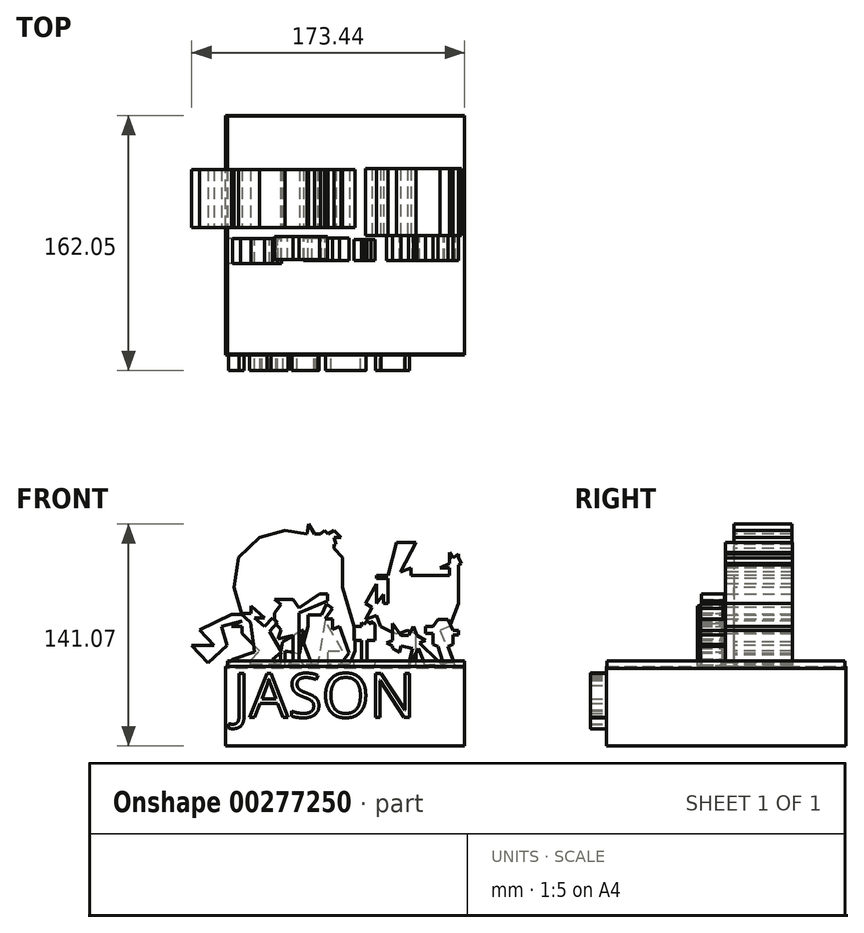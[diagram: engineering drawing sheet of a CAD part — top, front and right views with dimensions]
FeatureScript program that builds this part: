
annotation { "Feature Type Name" : "Feature", "Feature Type Description" : "" }
export const myFeature = defineFeature(function(context is Context, id is Id, definition is map)
    precondition{}
    {
        {
            var Q0;
            Q0=qCreatedBy(makeId("Front.planeOp"),FACE);
            var sketch = newSketch(context, id + "F0", { "sketchPlane" : qUnion([Q0])});
            skLineSegment(sketch, "E0.bottom", {"start": v(-75.76, -25.37) * mm, "end": v(76, -25.37) * mm});
            skLineSegment(sketch, "E0.top", {"start": v(-75.76, -75.88) * mm, "end": v(76, -75.88) * mm});
            skLineSegment(sketch, "E0.left", {"start": v(-75.76, -25.37) * mm, "end": v(-75.76, -75.88) * mm});
            skLineSegment(sketch, "E0.right", {"start": v(76, -25.37) * mm, "end": v(76, -75.88) * mm});
            skSolve(sketch);
        }
        {
            var Q0;
            Q0 = qSketchRegion(id + "F0", true);
            extrude(context, id + "F1", {"entities" : qUnion([Q0]), "depth" : 75.7 * mm, "hasSecondDirection" : true, "secondDirectionOppositeDirection" : true, "secondDirectionDepth" : 76.45 * mm});
        }
        {
            var Q0;
            Q0=qCreatedBy(makeId("Front.planeOp"),FACE);
            var sketch = newSketch(context, id + "F2", { "sketchPlane" : qUnion([Q0])});
            skLineSegment(sketch, "E1", {"start": v(-59.85, -23.92) * mm, "end": v(-59.85, -21.49) * mm});
            skLineSegment(sketch, "E2", {"start": v(-59.85, -21.49) * mm, "end": v(-54.02, -15.42) * mm});
            skLineSegment(sketch, "E3", {"start": v(-54.02, -15.42) * mm, "end": v(-65.45, -4.45) * mm});
            skLineSegment(sketch, "E4", {"start": v(-65.45, -4.45) * mm, "end": v(-65.45, 0) * mm});
            skLineSegment(sketch, "E5", {"start": v(-65.45, 0) * mm, "end": v(-71.9, 0) * mm});
            skLineSegment(sketch, "E6", {"start": v(-71.9, 0) * mm, "end": v(-65.45, 3.76) * mm});
            skLineSegment(sketch, "E7", {"start": v(-65.45, 3.76) * mm, "end": v(-78.3, 0) * mm});
            skLineSegment(sketch, "E8", {"start": v(-78.3, 0) * mm, "end": v(-74.8, -11.96) * mm});
            skLineSegment(sketch, "E9", {"start": v(-74.8, -11.96) * mm, "end": v(-86.8, -23.19) * mm});
            skLineSegment(sketch, "E10", {"start": v(-86.8, -23.19) * mm, "end": v(-97.31, -11.96) * mm});
            skLineSegment(sketch, "E11", {"start": v(-97.31, -11.96) * mm, "end": v(-82.92, -11.96) * mm});
            skLineSegment(sketch, "E12", {"start": v(-82.92, -11.96) * mm, "end": v(-92.3, -1.93) * mm});
            skLineSegment(sketch, "E13", {"start": v(-92.3, -1.93) * mm, "end": v(-71.9, 7.9) * mm});
            skLineSegment(sketch, "E14", {"start": v(-71.9, 7.9) * mm, "end": v(-65.45, 7.9) * mm});
            skLineSegment(sketch, "E15", {"start": v(-65.45, 7.9) * mm, "end": v(-70.43, 24.9) * mm});
            skLineSegment(sketch, "E16", {"start": v(-70.43, 24.9) * mm, "end": v(-67.62, 43.83) * mm});
            skLineSegment(sketch, "E17", {"start": v(-67.62, 43.83) * mm, "end": v(-54.02, 56.55) * mm});
            skLineSegment(sketch, "E18", {"start": v(-54.02, 56.55) * mm, "end": v(-38.04, 61.23) * mm});
            skLineSegment(sketch, "E19", {"start": v(-38.04, 61.23) * mm, "end": v(-24.16, 58.88) * mm});
            skLineSegment(sketch, "E20", {"start": v(-24.16, 58.88) * mm, "end": v(-23.1, 65.19) * mm});
            skLineSegment(sketch, "E21", {"start": v(-23.1, 65.19) * mm, "end": v(-19.41, 58.88) * mm});
            skLineSegment(sketch, "E22", {"start": v(-19.41, 58.88) * mm, "end": v(-15.5, 58.88) * mm});
            skLineSegment(sketch, "E23", {"start": v(-15.5, 58.88) * mm, "end": v(-13, 61.23) * mm});
            skLineSegment(sketch, "E24", {"start": v(-13, 61.23) * mm, "end": v(-10.8, 58.88) * mm});
            skLineSegment(sketch, "E25", {"start": v(-10.8, 58.88) * mm, "end": v(-6.78, 61.23) * mm});
            skLineSegment(sketch, "E26", {"start": v(-6.78, 61.23) * mm, "end": v(-2.4, 56.55) * mm});
            skLineSegment(sketch, "E27", {"start": v(-2.4, 56.55) * mm, "end": v(-6.78, 56.55) * mm});
            skLineSegment(sketch, "E28", {"start": v(-6.78, 56.55) * mm, "end": v(-5.55, 52.34) * mm});
            skLineSegment(sketch, "E29", {"start": v(-5.55, 52.34) * mm, "end": v(-6.78, 52.34) * mm});
            skLineSegment(sketch, "E30", {"start": v(-6.78, 52.34) * mm, "end": v(-6.78, 49.66) * mm});
            skLineSegment(sketch, "E31", {"start": v(-6.78, 49.66) * mm, "end": v(-1.33, 43.83) * mm});
            skLineSegment(sketch, "E32", {"start": v(-1.33, 43.83) * mm, "end": v(-1.33, 24.9) * mm});
            skLineSegment(sketch, "E33", {"start": v(-1.33, 24.9) * mm, "end": v(6.53, -1.93) * mm});
            skLineSegment(sketch, "E34", {"start": v(6.53, -1.93) * mm, "end": v(6.53, -15.42) * mm});
            skLineSegment(sketch, "E35", {"start": v(6.53, -15.42) * mm, "end": v(3.02, -23.92) * mm});
            skLineSegment(sketch, "E36", {"start": v(3.02, -23.92) * mm, "end": v(-10.8, -23.92) * mm});
            skLineSegment(sketch, "E37", {"start": v(-10.8, -23.92) * mm, "end": v(-10.8, -15.42) * mm});
            skLineSegment(sketch, "E38", {"start": v(-10.8, -15.42) * mm, "end": v(-1.33, -15.42) * mm});
            skLineSegment(sketch, "E39", {"start": v(-1.33, -15.42) * mm, "end": v(-12.52, 3.76) * mm});
            skLineSegment(sketch, "E40", {"start": v(-12.52, 3.76) * mm, "end": v(-17.2, -23.92) * mm});
            skLineSegment(sketch, "E41", {"start": v(-17.2, -23.92) * mm, "end": v(-38.04, -23.92) * mm});
            skLineSegment(sketch, "E42", {"start": v(-38.04, -23.92) * mm, "end": v(-38.04, -15.42) * mm});
            skLineSegment(sketch, "E43", {"start": v(-38.04, -15.42) * mm, "end": v(-28.87, -16.97) * mm});
            skLineSegment(sketch, "E44", {"start": v(-28.87, -16.97) * mm, "end": v(-26.32, -1.93) * mm});
            skLineSegment(sketch, "E45", {"start": v(-26.32, -1.93) * mm, "end": v(-39.52, -9.63) * mm});
            skLineSegment(sketch, "E46", {"start": v(-39.52, -9.63) * mm, "end": v(-40.93, -17.97) * mm});
            skLineSegment(sketch, "E47", {"start": v(-40.93, -17.97) * mm, "end": v(-40.93, -23.92) * mm});
            skLineSegment(sketch, "E48", {"start": v(-40.93, -23.92) * mm, "end": v(-59.85, -23.92) * mm});
            skSolve(sketch);
        }
        {
            var Q0;
            Q0 = qSketchRegion(id + "F2", true);
            extrude(context, id + "F3", {"entities" : qUnion([Q0]), "oppositeDirection" : true, "depth" : 42.16 * mm, "hasSecondDirection" : true, "secondDirectionOppositeDirection" : true, "secondDirectionDepth" : 5.33 * mm});
        }
        {
            var Q0;
            Q0=qCreatedBy(makeId("Front.planeOp"),FACE);
            var sketch = newSketch(context, id + "F4", { "sketchPlane" : qUnion([Q0])});
            skLineSegment(sketch, "E49", {"start": v(45.05, -25.13) * mm, "end": v(45.05, -4.74) * mm});
            skLineSegment(sketch, "E50", {"start": v(45.05, -4.74) * mm, "end": v(39.7, -2.3) * mm});
            skLineSegment(sketch, "E51", {"start": v(39.7, -2.3) * mm, "end": v(32.9, -4.74) * mm});
            skLineSegment(sketch, "E52", {"start": v(32.9, -4.74) * mm, "end": v(22.7, 0) * mm});
            skLineSegment(sketch, "E53", {"start": v(22.7, 0) * mm, "end": v(20.04, 7.16) * mm});
            skLineSegment(sketch, "E54", {"start": v(20.04, 7.16) * mm, "end": v(13.01, 4.54) * mm});
            skLineSegment(sketch, "E55", {"start": v(13.01, 4.54) * mm, "end": v(17.37, 12.26) * mm});
            skLineSegment(sketch, "E56", {"start": v(17.37, 12.26) * mm, "end": v(13.01, 14.72) * mm});
            skLineSegment(sketch, "E57", {"start": v(13.01, 14.72) * mm, "end": v(20.04, 27.17) * mm});
            skLineSegment(sketch, "E58", {"start": v(20.04, 27.17) * mm, "end": v(20.04, 14.72) * mm});
            skLineSegment(sketch, "E59", {"start": v(20.04, 14.72) * mm, "end": v(24.4, 20.52) * mm});
            skLineSegment(sketch, "E60", {"start": v(24.4, 20.52) * mm, "end": v(24.4, 14.72) * mm});
            skLineSegment(sketch, "E61", {"start": v(24.4, 14.72) * mm, "end": v(27.57, 14.72) * mm});
            skLineSegment(sketch, "E62", {"start": v(27.57, 14.72) * mm, "end": v(27.57, 30.47) * mm});
            skLineSegment(sketch, "E63", {"start": v(27.57, 30.47) * mm, "end": v(20.04, 30.47) * mm});
            skLineSegment(sketch, "E64", {"start": v(20.04, 30.47) * mm, "end": v(20.04, 32.66) * mm});
            skLineSegment(sketch, "E65", {"start": v(20.04, 32.66) * mm, "end": v(27.57, 32.66) * mm});
            skLineSegment(sketch, "E66", {"start": v(27.57, 32.66) * mm, "end": v(32.9, 53.54) * mm});
            skLineSegment(sketch, "E67", {"start": v(32.9, 53.54) * mm, "end": v(45.05, 53.54) * mm});
            skLineSegment(sketch, "E68", {"start": v(45.05, 53.54) * mm, "end": v(35.34, 34.6) * mm});
            skLineSegment(sketch, "E69", {"start": v(35.34, 34.6) * mm, "end": v(42.14, 37.27) * mm});
            skLineSegment(sketch, "E70", {"start": v(42.14, 37.27) * mm, "end": v(42.14, 32.66) * mm});
            skLineSegment(sketch, "E71", {"start": v(42.14, 32.66) * mm, "end": v(66.42, 32.66) * mm});
            skLineSegment(sketch, "E72", {"start": v(66.42, 32.66) * mm, "end": v(66.42, 37.27) * mm});
            skLineSegment(sketch, "E73", {"start": v(66.42, 37.27) * mm, "end": v(60.59, 37.27) * mm});
            skLineSegment(sketch, "E74", {"start": v(60.59, 37.27) * mm, "end": v(66.42, 40.19) * mm});
            skLineSegment(sketch, "E75", {"start": v(66.42, 40.19) * mm, "end": v(66.42, 46.99) * mm});
            skLineSegment(sketch, "E76", {"start": v(66.42, 46.99) * mm, "end": v(68.85, 43.59) * mm});
            skPoint(sketch, "E76.endSnap0", {"position": v(66.42, 43.59) * mm});
            skLineSegment(sketch, "E77", {"start": v(68.85, 43.59) * mm, "end": v(72.31, 46.06) * mm});
            skLineSegment(sketch, "E78", {"start": v(72.31, 46.06) * mm, "end": v(72.31, 43.59) * mm});
            skLineSegment(sketch, "E79", {"start": v(72.31, 43.59) * mm, "end": v(74.19, 40.19) * mm});
            skLineSegment(sketch, "E80", {"start": v(74.19, 40.19) * mm, "end": v(72.31, 39.15) * mm});
            skLineSegment(sketch, "E81", {"start": v(72.31, 39.15) * mm, "end": v(72.31, 32.66) * mm});
            skLineSegment(sketch, "E82", {"start": v(72.31, 32.66) * mm, "end": v(72.31, 14.72) * mm});
            skLineSegment(sketch, "E83", {"start": v(72.31, 14.72) * mm, "end": v(66.42, 0) * mm});
            skLineSegment(sketch, "E84", {"start": v(66.42, 0) * mm, "end": v(60.59, -2.3) * mm});
            skLineSegment(sketch, "E85", {"start": v(60.59, -2.3) * mm, "end": v(68.85, -23.16) * mm});
            skLineSegment(sketch, "E86", {"start": v(68.85, -23.16) * mm, "end": v(45.05, -25.13) * mm});
            skSolve(sketch);
        }
        {
            var Q0;
            Q0 = qSketchRegion(id + "F4", true);
            extrude(context, id + "F5", {"entities" : qUnion([Q0]), "oppositeDirection" : true, "depth" : 42.67 * mm});
        }
        {
            var Q0;
            Q0=qCreatedBy(makeId("Front.planeOp"),FACE);
            var sketch = newSketch(context, id + "F6", { "sketchPlane" : qUnion([Q0])});
            skLineSegment(sketch, "E87", {"start": v(70.3, -25.62) * mm, "end": v(65.45, -12.5) * mm});
            skLineSegment(sketch, "E88", {"start": v(65.45, -12.5) * mm, "end": v(68.74, -11.28) * mm});
            skLineSegment(sketch, "E89", {"start": v(68.74, -11.28) * mm, "end": v(68.74, -5.22) * mm});
            skLineSegment(sketch, "E90", {"start": v(68.74, -5.22) * mm, "end": v(72.25, -5.22) * mm});
            skLineSegment(sketch, "E91", {"start": v(72.25, -5.22) * mm, "end": v(72.25, -2.3) * mm});
            skLineSegment(sketch, "E92", {"start": v(72.25, -2.3) * mm, "end": v(68.74, -2.3) * mm});
            skLineSegment(sketch, "E93", {"start": v(68.74, -2.3) * mm, "end": v(65.45, 4.74) * mm});
            skLineSegment(sketch, "E94", {"start": v(65.45, 4.74) * mm, "end": v(59.13, 4.74) * mm});
            skLineSegment(sketch, "E95", {"start": v(59.13, 4.74) * mm, "end": v(55.98, 0) * mm});
            skLineSegment(sketch, "E96", {"start": v(55.98, 0) * mm, "end": v(51.12, 0) * mm});
            skLineSegment(sketch, "E97", {"start": v(51.12, 0) * mm, "end": v(51.12, -4.25) * mm});
            skLineSegment(sketch, "E98", {"start": v(51.12, -4.25) * mm, "end": v(55.98, -4.25) * mm});
            skLineSegment(sketch, "E99", {"start": v(55.98, -4.25) * mm, "end": v(55.98, -11.28) * mm});
            skLineSegment(sketch, "E100", {"start": v(55.98, -11.28) * mm, "end": v(59.13, -12.5) * mm});
            skLineSegment(sketch, "E101", {"start": v(59.13, -12.5) * mm, "end": v(63.26, -25.37) * mm});
            skLineSegment(sketch, "E102", {"start": v(63.26, -25.37) * mm, "end": v(70.3, -25.62) * mm});
            skSolve(sketch);
        }
        {
            var Q0;
            Q0 = qSketchRegion(id + "F6", true);
            extrude(context, id + "F7", {"entities" : qUnion([Q0]), "depth" : 15.75 * mm});
        }
        {
            var Q0;
            Q0=qCreatedBy(makeId("Front.planeOp"),FACE);
            var sketch = newSketch(context, id + "F8", { "sketchPlane" : qUnion([Q0])});
            skLineSegment(sketch, "E103", {"start": v(51.6, -26.1) * mm, "end": v(46.75, -13.96) * mm});
            skLineSegment(sketch, "E104", {"start": v(46.75, -13.96) * mm, "end": v(40.44, -25.13) * mm});
            skLineSegment(sketch, "E105", {"start": v(40.44, -25.13) * mm, "end": v(42.86, -13.96) * mm});
            skLineSegment(sketch, "E106", {"start": v(42.86, -13.96) * mm, "end": v(35.59, -12.38) * mm});
            skLineSegment(sketch, "E107", {"start": v(35.59, -12.38) * mm, "end": v(34.7, -16.46) * mm});
            skLineSegment(sketch, "E108", {"start": v(34.7, -16.46) * mm, "end": v(30.27, -13.96) * mm});
            skLineSegment(sketch, "E109", {"start": v(30.27, -13.96) * mm, "end": v(30.27, -12.38) * mm});
            skLineSegment(sketch, "E110", {"start": v(30.27, -12.38) * mm, "end": v(26.5, -10.25) * mm});
            skLineSegment(sketch, "E111", {"start": v(26.5, -10.25) * mm, "end": v(30.27, -8.74) * mm});
            skLineSegment(sketch, "E112", {"start": v(30.27, -8.74) * mm, "end": v(30.27, 2.06) * mm});
            skLineSegment(sketch, "E113", {"start": v(30.27, 2.06) * mm, "end": v(35.59, -5.7) * mm});
            skLineSegment(sketch, "E114", {"start": v(35.59, -5.7) * mm, "end": v(40.44, -5.7) * mm});
            skLineSegment(sketch, "E115", {"start": v(40.44, -5.7) * mm, "end": v(43.66, 0) * mm});
            skLineSegment(sketch, "E116", {"start": v(43.66, 0) * mm, "end": v(45.94, -5.7) * mm});
            skLineSegment(sketch, "E117", {"start": v(45.94, -5.7) * mm, "end": v(51.3, -8.74) * mm});
            skLineSegment(sketch, "E118", {"start": v(51.3, -8.74) * mm, "end": v(47.53, -10.25) * mm});
            skLineSegment(sketch, "E119", {"start": v(47.53, -10.25) * mm, "end": v(62.53, -25.13) * mm});
            skLineSegment(sketch, "E120", {"start": v(62.53, -25.13) * mm, "end": v(51.6, -26.1) * mm});
            skSolve(sketch);
        }
        {
            var Q0;
            Q0 = qSketchRegion(id + "F8", true);
            extrude(context, id + "F9", {"entities" : qUnion([Q0]), "depth" : 15.75 * mm});
        }
        {
            var Q0;
            Q0=qCreatedBy(makeId("Front.planeOp"),FACE);
            var sketch = newSketch(context, id + "F10", { "sketchPlane" : qUnion([Q0])});
            skLineSegment(sketch, "E121", {"start": v(5.71, -25.37) * mm, "end": v(5.71, -21.98) * mm});
            skLineSegment(sketch, "E122", {"start": v(5.71, -21.98) * mm, "end": v(10.57, -21.98) * mm});
            skLineSegment(sketch, "E123", {"start": v(10.57, -21.98) * mm, "end": v(10.57, -8.86) * mm});
            skLineSegment(sketch, "E124", {"start": v(10.57, -8.86) * mm, "end": v(5.71, -8.86) * mm});
            skLineSegment(sketch, "E125", {"start": v(5.71, -8.86) * mm, "end": v(5.71, 0) * mm});
            skLineSegment(sketch, "E126", {"start": v(5.71, 0) * mm, "end": v(10.57, 0) * mm});
            skLineSegment(sketch, "E127", {"start": v(10.57, 0) * mm, "end": v(10.57, 2.8) * mm});
            skLineSegment(sketch, "E128", {"start": v(10.57, 2.8) * mm, "end": v(13.73, 0) * mm});
            skLineSegment(sketch, "E129", {"start": v(13.73, 0) * mm, "end": v(12.15, 1.4) * mm});
            skLineSegment(sketch, "E130", {"start": v(12.15, 1.4) * mm, "end": v(14.1, 3.61) * mm});
            skLineSegment(sketch, "E131", {"start": v(14.1, 3.61) * mm, "end": v(16.61, 1.4) * mm});
            skLineSegment(sketch, "E132", {"start": v(16.61, 1.4) * mm, "end": v(16.61, 3.61) * mm});
            skLineSegment(sketch, "E133", {"start": v(16.61, 3.61) * mm, "end": v(19.12, 1.4) * mm});
            skLineSegment(sketch, "E134", {"start": v(19.12, 1.4) * mm, "end": v(19.12, -8.86) * mm});
            skLineSegment(sketch, "E135", {"start": v(19.12, -8.86) * mm, "end": v(14.1, -8.86) * mm});
            skLineSegment(sketch, "E136", {"start": v(14.1, -8.86) * mm, "end": v(14.1, -21.98) * mm});
            skLineSegment(sketch, "E137", {"start": v(14.1, -21.98) * mm, "end": v(19.12, -21.98) * mm});
            skLineSegment(sketch, "E138", {"start": v(19.12, -21.98) * mm, "end": v(18.82, -24.65) * mm});
            skLineSegment(sketch, "E139", {"start": v(18.82, -24.65) * mm, "end": v(5.71, -25.37) * mm});
            skSolve(sketch);
        }
        {
            var Q0;
            Q0 = qSketchRegion(id + "F10", true);
            extrude(context, id + "F11", {"entities" : qUnion([Q0]), "operationType" : NewBodyOperationType.ADD, "depth" : 15.75 * mm, "hasSecondDirection" : true, "secondDirectionOppositeDirection" : false, "secondDirectionDepth" : 2.54 * mm});
        }
        {
            var Q0;
            Q0=qCreatedBy(makeId("Front.planeOp"),FACE);
            var sketch = newSketch(context, id + "F12", { "sketchPlane" : qUnion([Q0])});
            skLineSegment(sketch, "E140", {"start": v(-3.52, -24.89) * mm, "end": v(2.8, -16.63) * mm});
            skLineSegment(sketch, "E141", {"start": v(2.8, -16.63) * mm, "end": v(-3.27, 0) * mm});
            skLineSegment(sketch, "E142", {"start": v(-3.27, 0) * mm, "end": v(-7.8, -1.65) * mm});
            skLineSegment(sketch, "E143", {"start": v(-7.8, -1.65) * mm, "end": v(-7.8, 4.98) * mm});
            skLineSegment(sketch, "E144", {"start": v(-7.8, 4.98) * mm, "end": v(-12.74, 4.98) * mm});
            skLineSegment(sketch, "E145", {"start": v(-12.74, 4.98) * mm, "end": v(-7.8, 11.45) * mm});
            skLineSegment(sketch, "E146", {"start": v(-7.8, 11.45) * mm, "end": v(-11.59, 14.35) * mm});
            skLineSegment(sketch, "E147", {"start": v(-11.59, 14.35) * mm, "end": v(-14.69, 7.4) * mm});
            skLineSegment(sketch, "E148", {"start": v(-14.69, 7.4) * mm, "end": v(-23.43, 7.4) * mm});
            skLineSegment(sketch, "E149", {"start": v(-23.43, 7.4) * mm, "end": v(-23.43, 0) * mm});
            skLineSegment(sketch, "E150", {"start": v(-23.43, 0) * mm, "end": v(-26.1, -10.32) * mm});
            skLineSegment(sketch, "E151", {"start": v(-26.1, -10.32) * mm, "end": v(-20.76, -24.89) * mm});
            skLineSegment(sketch, "E152", {"start": v(-20.76, -24.89) * mm, "end": v(-3.52, -24.89) * mm});
            skSolve(sketch);
        }
        {
            var Q0;
            Q0 = qSketchRegion(id + "F12", true);
            extrude(context, id + "F13", {"entities" : qUnion([Q0]), "operationType" : NewBodyOperationType.ADD, "depth" : 15.75 * mm, "hasSecondDirection" : true, "secondDirectionOppositeDirection" : false, "secondDirectionDepth" : 1.52 * mm});
        }
        {
            var Q0;
            Q0=qCreatedBy(makeId("Front.planeOp"),FACE);
            var sketch = newSketch(context, id + "F14", { "sketchPlane" : qUnion([Q0])});
            skLineSegment(sketch, "E153", {"start": v(-25.86, -24.4) * mm, "end": v(-29.01, -20.52) * mm});
            skLineSegment(sketch, "E154", {"start": v(-29.01, -20.52) * mm, "end": v(-29.01, 8.86) * mm});
            skLineSegment(sketch, "E155", {"start": v(-29.01, 8.86) * mm, "end": v(-11.04, 16.4) * mm});
            skLineSegment(sketch, "E156", {"start": v(-11.04, 16.4) * mm, "end": v(-11.04, 20.76) * mm});
            skLineSegment(sketch, "E157", {"start": v(-11.04, 20.76) * mm, "end": v(-16.14, 20.76) * mm});
            skLineSegment(sketch, "E158", {"start": v(-16.14, 20.76) * mm, "end": v(-29.01, 11.78) * mm});
            skLineSegment(sketch, "E159", {"start": v(-29.01, 11.78) * mm, "end": v(-32.9, 17.34) * mm});
            skLineSegment(sketch, "E160", {"start": v(-32.9, 17.34) * mm, "end": v(-38, 17.34) * mm});
            skLineSegment(sketch, "E161", {"start": v(-38, 17.34) * mm, "end": v(-44.55, 17.34) * mm});
            skPoint(sketch, "E161.endSnap0", {"position": v(-35.45, 17.34) * mm});
            skLineSegment(sketch, "E162", {"start": v(-44.55, 17.34) * mm, "end": v(-40.42, 14.2) * mm});
            skLineSegment(sketch, "E163", {"start": v(-40.42, 14.2) * mm, "end": v(-44.55, 8.86) * mm});
            skLineSegment(sketch, "E164", {"start": v(-44.55, 8.86) * mm, "end": v(-44.55, 2.55) * mm});
            skLineSegment(sketch, "E165", {"start": v(-44.55, 2.55) * mm, "end": v(-40.42, -2.06) * mm});
            skLineSegment(sketch, "E166", {"start": v(-40.42, -2.06) * mm, "end": v(-42.37, -7.65) * mm});
            skLineSegment(sketch, "E167", {"start": v(-42.37, -7.65) * mm, "end": v(-32.9, -5.67) * mm});
            skLineSegment(sketch, "E168", {"start": v(-34.35, -5.7) * mm, "end": v(-38, -2.06) * mm});
            skLineSegment(sketch, "E169", {"start": v(-37.27, -2.06) * mm, "end": v(-32.9, 6.04) * mm});
            skLineSegment(sketch, "E170", {"start": v(-32.9, 6.04) * mm, "end": v(-32.9, -5.67) * mm});
            skLineSegment(sketch, "E171", {"start": v(-32.9, -5.67) * mm, "end": v(-32.9, -20.52) * mm});
            skLineSegment(sketch, "E172", {"start": v(-32.9, -20.52) * mm, "end": v(-36.3, -25.13) * mm});
            skLineSegment(sketch, "E173", {"start": v(-36.3, -25.13) * mm, "end": v(-25.86, -24.4) * mm});
            skSolve(sketch);
        }
        {
            var Q0;
            Q0 = qSketchRegion(id + "F14", true);
            extrude(context, id + "F15", {"entities" : qUnion([Q0]), "operationType" : NewBodyOperationType.ADD, "depth" : 15.24 * mm, "hasSecondDirection" : true, "secondDirectionOppositeDirection" : false, "secondDirectionDepth" : 0.5 * mm});
        }
        {
            var Q0;
            Q0=qCreatedBy(makeId("Front.planeOp"),FACE);
            var sketch = newSketch(context, id + "F16", { "sketchPlane" : qUnion([Q0])});
            skLineSegment(sketch, "E174", {"start": v(-42.6, -24.89) * mm, "end": v(-46, -20.76) * mm});
            skLineSegment(sketch, "E175", {"start": v(-46, -20.76) * mm, "end": v(-40.11, -15.9) * mm});
            skLineSegment(sketch, "E176", {"start": v(-40.11, -15.9) * mm, "end": v(-47.95, -3.04) * mm});
            skLineSegment(sketch, "E177", {"start": v(-47.95, -3.04) * mm, "end": v(-42.85, 2.8) * mm});
            skLineSegment(sketch, "E178", {"start": v(-42.85, 2.8) * mm, "end": v(-46, 5.55) * mm});
            skLineSegment(sketch, "E179", {"start": v(-46, 5.55) * mm, "end": v(-50.87, 0) * mm});
            skLineSegment(sketch, "E180", {"start": v(-50.87, 0) * mm, "end": v(-57.22, 5.55) * mm});
            skLineSegment(sketch, "E181", {"start": v(-57.22, 5.55) * mm, "end": v(-50.87, 5.55) * mm});
            skLineSegment(sketch, "E182", {"start": v(-50.87, 5.55) * mm, "end": v(-59.7, 13.27) * mm});
            skLineSegment(sketch, "E183", {"start": v(-59.7, 13.27) * mm, "end": v(-59.7, 8.38) * mm});
            skLineSegment(sketch, "E184", {"start": v(-59.7, 8.38) * mm, "end": v(-66.16, 8.38) * mm});
            skLineSegment(sketch, "E185", {"start": v(-66.16, 8.38) * mm, "end": v(-59.78, 2.8) * mm});
            skLineSegment(sketch, "E186", {"start": v(-59.78, 2.8) * mm, "end": v(-57.22, -15.9) * mm});
            skLineSegment(sketch, "E187", {"start": v(-57.22, -15.9) * mm, "end": v(-51.67, -20.76) * mm});
            skLineSegment(sketch, "E188", {"start": v(-51.67, -20.76) * mm, "end": v(-57.22, -24.65) * mm});
            skLineSegment(sketch, "E189", {"start": v(-57.22, -24.65) * mm, "end": v(-42.6, -24.89) * mm});
            skLineSegment(sketch, "E190", {"start": v(-57.22, -15.9) * mm, "end": v(-71.26, -20.76) * mm});
            skLineSegment(sketch, "E191", {"start": v(-71.26, -20.76) * mm, "end": v(-74.87, -24.89) * mm});
            skLineSegment(sketch, "E192", {"start": v(-74.87, -24.89) * mm, "end": v(-57.22, -24.65) * mm});
            skLineSegment(sketch, "E193", {"start": v(-58.15, -24.65) * mm, "end": v(-51.67, -20.76) * mm});
            skLineSegment(sketch, "E194", {"start": v(-51.67, -20.76) * mm, "end": v(-57.22, -15.9) * mm});
            skSolve(sketch);
        }
        {
            var Q0;
            Q0 = qSketchRegion(id + "F16", true);
            extrude(context, id + "F17", {"entities" : qUnion([Q0]), "operationType" : NewBodyOperationType.ADD, "depth" : 17.78 * mm, "hasSecondDirection" : true, "secondDirectionOppositeDirection" : false, "secondDirectionDepth" : 1.78 * mm});
        }
        {
            var Q0;
            Q0=qCreatedBy(makeId("Front.planeOp"),FACE);
            var sketch = newSketch(context, id + "F18", { "sketchPlane" : qUnion([Q0])});
            skText(sketch, "E195", { "text": "JASON\n", "fontName": "OpenSans-Regular.ttf"});
            const initialGuessF18  = {"E195": [-0.0709, -0.05757, 1, 0, 0.02798]};
            skSetInitialGuess(sketch, initialGuessF18);
            skSolve(sketch);
        }
        {
            var Q0;
            Q0=makeQuery(id+"F18.imprint","IMPRINT",FACE,{"disambiguationData":[TD([[makeQuery(id+"F18.imprint","IMPRINT",EDGE,{"derivedFrom":sQuery(id+"F18.wireOp",EDGE,"E195.sketch_text.stroke-0")}),-1.0]])]});
            var Q1;
            Q1=makeQuery(id+"F18.imprint","IMPRINT",FACE,{"disambiguationData":[TD([[makeQuery(id+"F18.imprint","IMPRINT",EDGE,{"derivedFrom":sQuery(id+"F18.wireOp",EDGE,"E195.sketch_text.stroke-23")}),-1.0]])]});
            var Q2;
            Q2=makeQuery(id+"F18.imprint","IMPRINT",FACE,{"disambiguationData":[TD([[makeQuery(id+"F18.imprint","IMPRINT",EDGE,{"derivedFrom":sQuery(id+"F18.wireOp",EDGE,"E195.sketch_text.stroke-64")}),-1.0]])]});
            var Q3;
            Q3=makeQuery(id+"F18.imprint","IMPRINT",FACE,{"disambiguationData":[TD([[makeQuery(id+"F18.imprint","IMPRINT",EDGE,{"derivedFrom":sQuery(id+"F18.wireOp",EDGE,"E195.sketch_text.stroke-10")}),-1.0]])]});
            var Q4;
            Q4=makeQuery(id+"F18.imprint","IMPRINT",FACE,{"disambiguationData":[TD([[makeQuery(id+"F18.imprint","IMPRINT",EDGE,{"derivedFrom":sQuery(id+"F18.wireOp",EDGE,"E195.sketch_text.stroke-48")}),-1.0]])]});
            var Q5;
            Q5 = qSketchRegion(id + "F18", true);
            extrude(context, id + "F19", {"entities" : qUnion([Q0, Q1, Q2, Q3, Q4, Q5]), "operationType" : NewBodyOperationType.ADD, "depth" : 85.6 * mm});
        }
        {
            var Q0;
            Q0=qCreatedBy(makeId("Front.planeOp"),FACE);
            var sketch = newSketch(context, id + "F20", { "sketchPlane" : qUnion([Q0])});
            skLineSegment(sketch, "E196.bottom", {"start": v(5, -26.46) * mm, "end": v(-74.56, -26.46) * mm});
            skLineSegment(sketch, "E196.top", {"start": v(5, -21.71) * mm, "end": v(-74.56, -21.71) * mm});
            skLineSegment(sketch, "E196.left", {"start": v(5, -26.46) * mm, "end": v(5, -21.71) * mm});
            skLineSegment(sketch, "E196.right", {"start": v(-74.56, -26.46) * mm, "end": v(-74.56, -21.71) * mm});
            skLineSegment(sketch, "E197.bottom", {"start": v(5, -26.46) * mm, "end": v(76.13, -26.46) * mm});
            skLineSegment(sketch, "E197.top", {"start": v(5, -21.71) * mm, "end": v(76.13, -21.71) * mm});
            skLineSegment(sketch, "E197.right", {"start": v(76.13, -26.46) * mm, "end": v(76.13, -21.71) * mm});
            skSolve(sketch);
        }
        {
            var Q0;
            Q0 = qSketchRegion(id + "F20", true);
            extrude(context, id + "F21", {"entities" : qUnion([Q0]), "oppositeDirection" : true, "depth" : 75.95 * mm, "hasSecondDirection" : true, "secondDirectionOppositeDirection" : false, "secondDirectionDepth" : 75.18 * mm});
        }
    });
